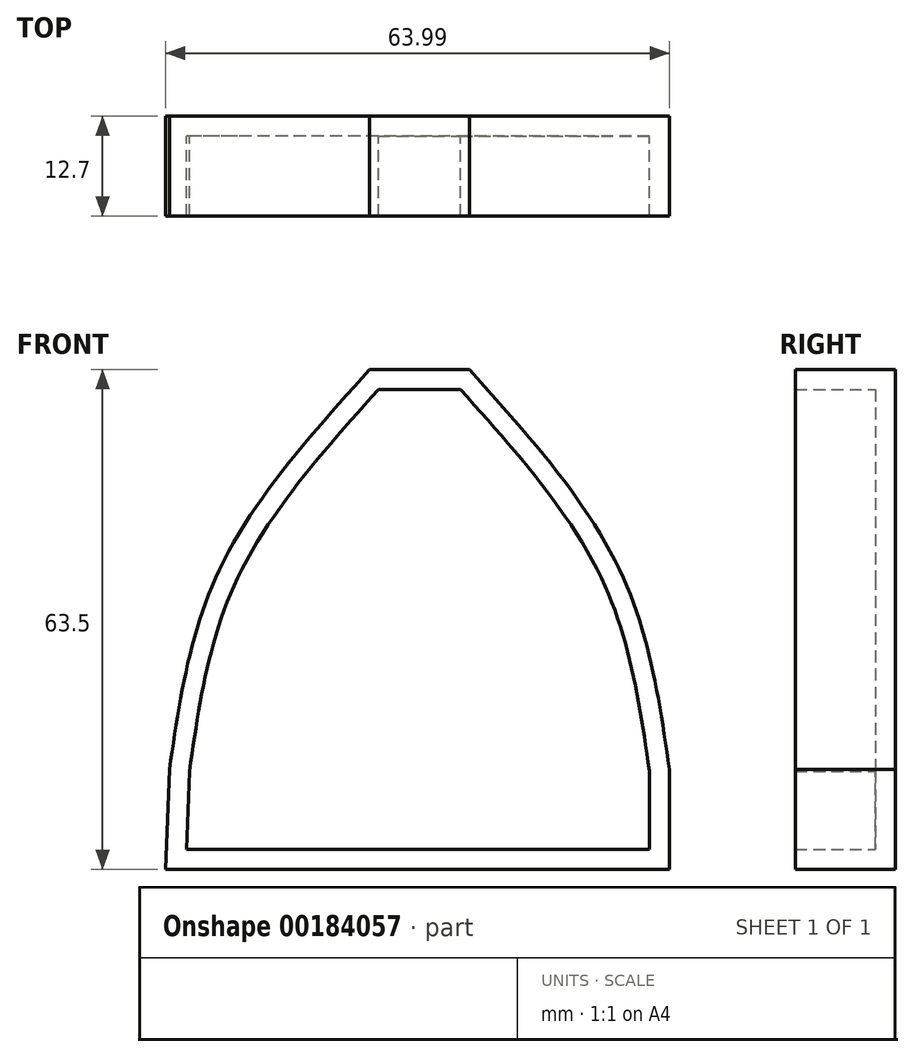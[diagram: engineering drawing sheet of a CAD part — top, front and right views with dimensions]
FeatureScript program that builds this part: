
annotation { "Feature Type Name" : "Feature", "Feature Type Description" : "" }
export const myFeature = defineFeature(function(context is Context, id is Id, definition is map)
    precondition{}
    {
        {
            var Q0;
            Q0=qCreatedBy(makeId("Front.planeOp"),FACE);
            var sketch = newSketch(context, id + "F0", { "sketchPlane" : qUnion([Q0])});
            skPoint(sketch, "E0", {"position": v(-32.24, 0) * mm});
            skPoint(sketch, "E1", {"position": v(31.75, 0) * mm});
            skLineSegment(sketch, "E2", {"start": v(31.75, 0) * mm, "end": v(-32.24, 0) * mm});
            skLineSegment(sketch, "E3", {"start": v(31.75, 0) * mm, "end": v(31.75, 12.7) * mm});
            skLineSegment(sketch, "E4", {"start": v(0, 0) * mm, "end": v(0, 63.5) * mm});
            skLineSegment(sketch, "E5", {"start": v(0, 0) * mm, "end": v(0, 38.1) * mm});
            skLineSegment(sketch, "E6", {"start": v(0, 38.1) * mm, "end": v(25.4, 38.1) * mm});
            skLineSegment(sketch, "E7", {"start": v(25.4, 38.1) * mm, "end": v(-25.4, 38.1) * mm});
            skLineSegment(sketch, "E8", {"start": v(0, 63.5) * mm, "end": v(6.35, 63.5) * mm});
            skLineSegment(sketch, "E9", {"start": v(6.35, 63.5) * mm, "end": v(-6.35, 63.5) * mm});
            skFitSpline(sketch, "E10", {"points": [v(-6.35, 63.5) * mm, v(-25.4, 38.1) * mm, v(-31.75, 12.7) * mm], "startDerivative": vector(-42.38, -47.18) * mm, "endDerivative": vector(-7.87, -54.54) * mm});
            skFitSpline(sketch, "E11", {"points": [v(6.35, 63.5) * mm, v(25.4, 38.1) * mm, v(31.75, 12.7) * mm], "startDerivative": vector(42.38, -47.18) * mm, "endDerivative": vector(7.87, -54.54) * mm});
            skLineSegment(sketch, "E12", {"start": v(-31.75, 12.7) * mm, "end": v(-32.24, 0) * mm});
            skSolve(sketch);
        }
        {
            var Q0;
            Q0 = qSketchRegion(id + "F0", true);
            extrude(context, id + "F1", {"entities" : qUnion([Q0]), "depth" : 12.7 * mm});
        }
        {
            var Q0;
            Q0=makeQuery(id+"F1.opExtrude","CAP_FACE",FACE,{"disambiguationData":[OSD([sQuery(id+"F0.wireOp",EDGE,"b8a19f53-8217-4763-9e69-421f62d43a0a"),sQuery(id+"F0.wireOp",EDGE,"42wohN06-ZgwP-yjYr-TY5Q-MqT3CEB3C7VW"),sQuery(id+"F0.wireOp",EDGE,"E3"),sQuery(id+"F0.wireOp",EDGE,"E9"),sQuery(id+"F0.wireOp",EDGE,"E10"),sQuery(id+"F0.wireOp",EDGE,"E11")])],"isStart":false});
            shell(context, id + "F2", {"entities" : qUnion([Q0]), "thickness" : 2.54 * mm});
        }
    });
